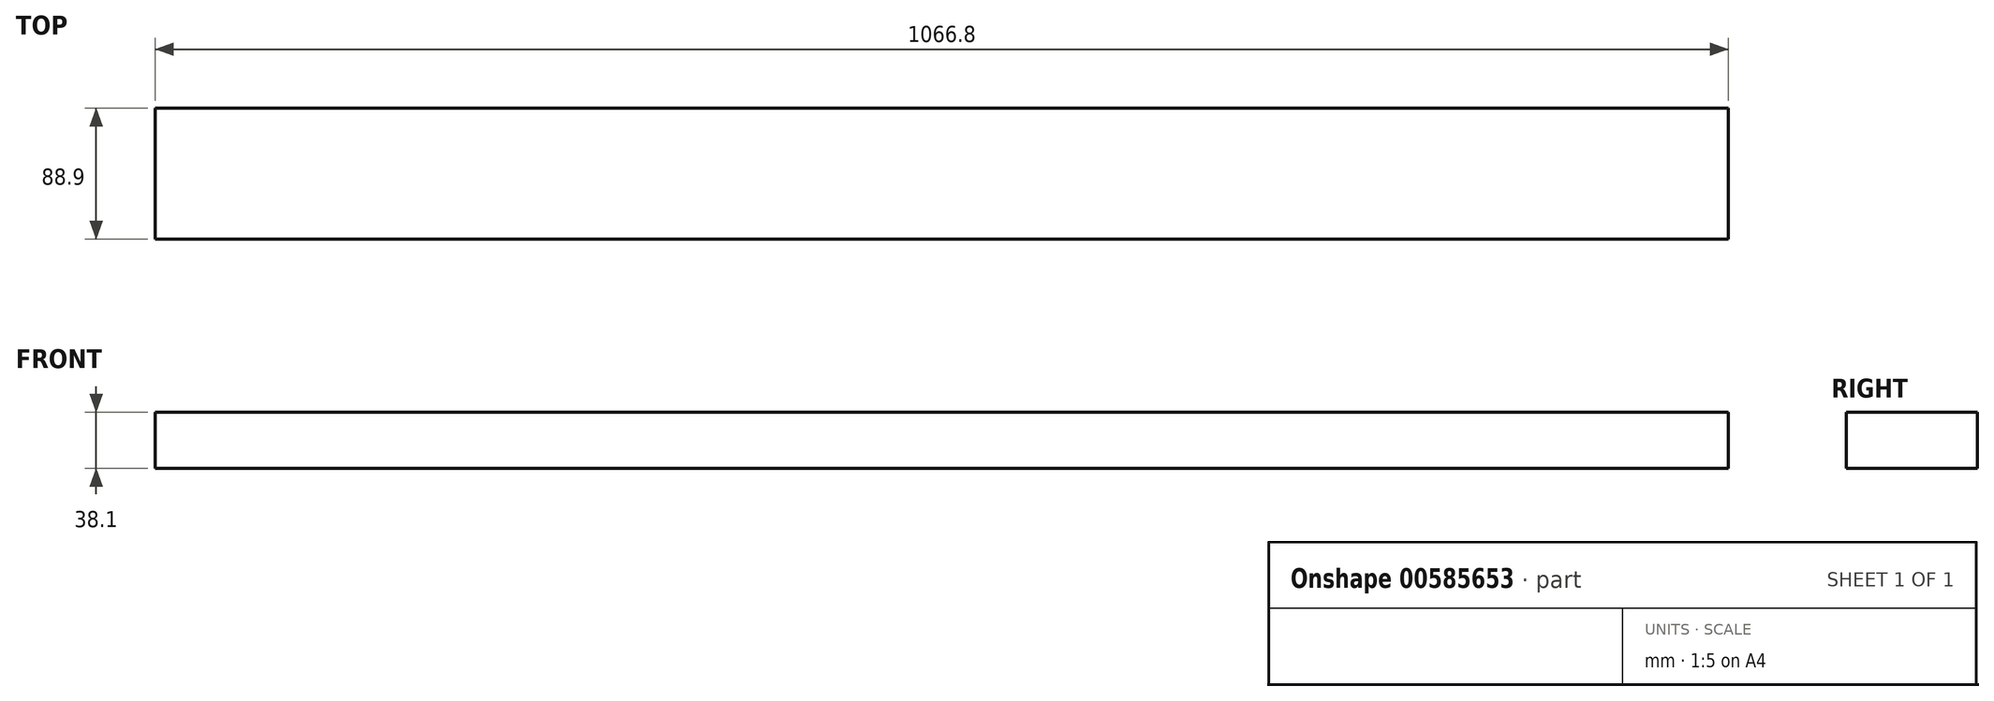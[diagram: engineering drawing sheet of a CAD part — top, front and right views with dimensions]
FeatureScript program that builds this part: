
annotation { "Feature Type Name" : "Feature", "Feature Type Description" : "" }
export const myFeature = defineFeature(function(context is Context, id is Id, definition is map)
    precondition{}
    {
        {
            var Q0;
            Q0=qCreatedBy(makeId("Right.planeOp"),FACE);
            var sketch = newSketch(context, id + "F0", { "sketchPlane" : qUnion([Q0])});
            skLineSegment(sketch, "E0.bottom", {"start": v(0, 0) * mm, "end": v(88.9, 0) * mm});
            skLineSegment(sketch, "E0.top", {"start": v(0, 38.1) * mm, "end": v(88.9, 38.1) * mm});
            skLineSegment(sketch, "E0.left", {"start": v(0, 0) * mm, "end": v(0, 38.1) * mm});
            skLineSegment(sketch, "E0.right", {"start": v(88.9, 0) * mm, "end": v(88.9, 38.1) * mm});
            skSolve(sketch);
        }
        {
            var Q0;
            Q0=qSketchRegion(id+"F0",true);
            extrude(context, id + "F1", {"entities" : qUnion([Q0]), "oppositeDirection" : true, "depth" : 1066.8 * mm, "offsetDistance" : 25.4 * mm});
        }
    });
